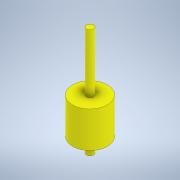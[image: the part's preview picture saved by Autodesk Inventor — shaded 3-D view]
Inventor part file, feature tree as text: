
AUTODESK INVENTOR PART (.ipt)
format: ipt  version: 2020.2 (Build 242310000, 310)  size: 117,760 bytes
history: native  units: mm
features: extrude x2, sketch x2
ambient origin geometry x8: Origin, YZ Plane, XZ Plane, XY Plane, X Axis, Y Axis, Z Axis, Center Point
bodies: Solido1 (feature_tree)
feature tree (4):
  extrude  "Estrusione1"  Depth=29.0mm
  extrude  "Estrusione2"  Depth=30.0mm TaperAngle=0.0deg
  sketch  "Schizzo1"
  sketch  "Schizzo2"
